# Revit family: Shower-Base-KOHLER-Archer-K-9395
name_source: partatom
category: Plumbing Fixtures
revit_build: Autodesk Revit 2017 (Build: 20160225_1515(x64)
units: mm (PartAtom-declared; Revit-internal decimal feet)

## family parameters
Cut with Voids When Loaded = No
Host = Face
OmniClass Number = 23.31.17.15
OmniClass Title = Shower Enclosure Bases
Part Type = Normal
Room Calculation Point = No
Round Connector Dimension = Use Diameter
Shared = No

## types (6) — shared parameters
ADA Compliant = No
Assembly Code = D2010700
CW Connection = No
Cold Water Inlet = Cold Water Inlet
Date Modified = 08/26/2020
Default Elevation = 0"
Description = 60inch x 60inch Single threshold center drain shower base with removable cover
Drain Included = No
HW Connection = No
Height = 4 3/16"
Hot Water Inlet = Hot Water Inlet
Length = 60"
Manufacturer = KOHLER Co.
Master Format 2014 = 22 42 23
Master Format 2014 Name = Residential Showers
Material = Acrylic
Product Documentation Link = https://www.us.kohler.com
Product Name = Archer
Product Page URL = http://www.us.kohler.com
URL = https://www.us.kohler.com
Vent Connection = No
Waste Connection = Yes
Waste Water Outlet = Waste Water Outlet
WaterSense Certified = No
Width = 60"

## per-type parameters (varying)
| type | Finish | Model | Type |
| 0-White | KOHLER-Acrylic-0-White | K-9395-0 | 1 |
| 96-Biscuit | KOHLER-Acrylic-96-Biscuit | K-9395-96 | 2 |
| NY-Dune | KOHLER-Acrylic-NY-Dune | K-9395-NY | 3 |
| 58-Thunder Grey | KOHLER-Acrylic-58-Thunder_Grey | K-9395-58 | 4 |
| 7-Black Black | KOHLER-Acrylic-7-Black_Black | K-9395-7 | 5 |
| 95-Ice Grey | KOHLER-Acrylic-95-Ice_Grey | K-9395-95 | 6 |

## geometry (parser evidence)
native form markers: Sweep x6
no freeform markers — native parametric forms only
